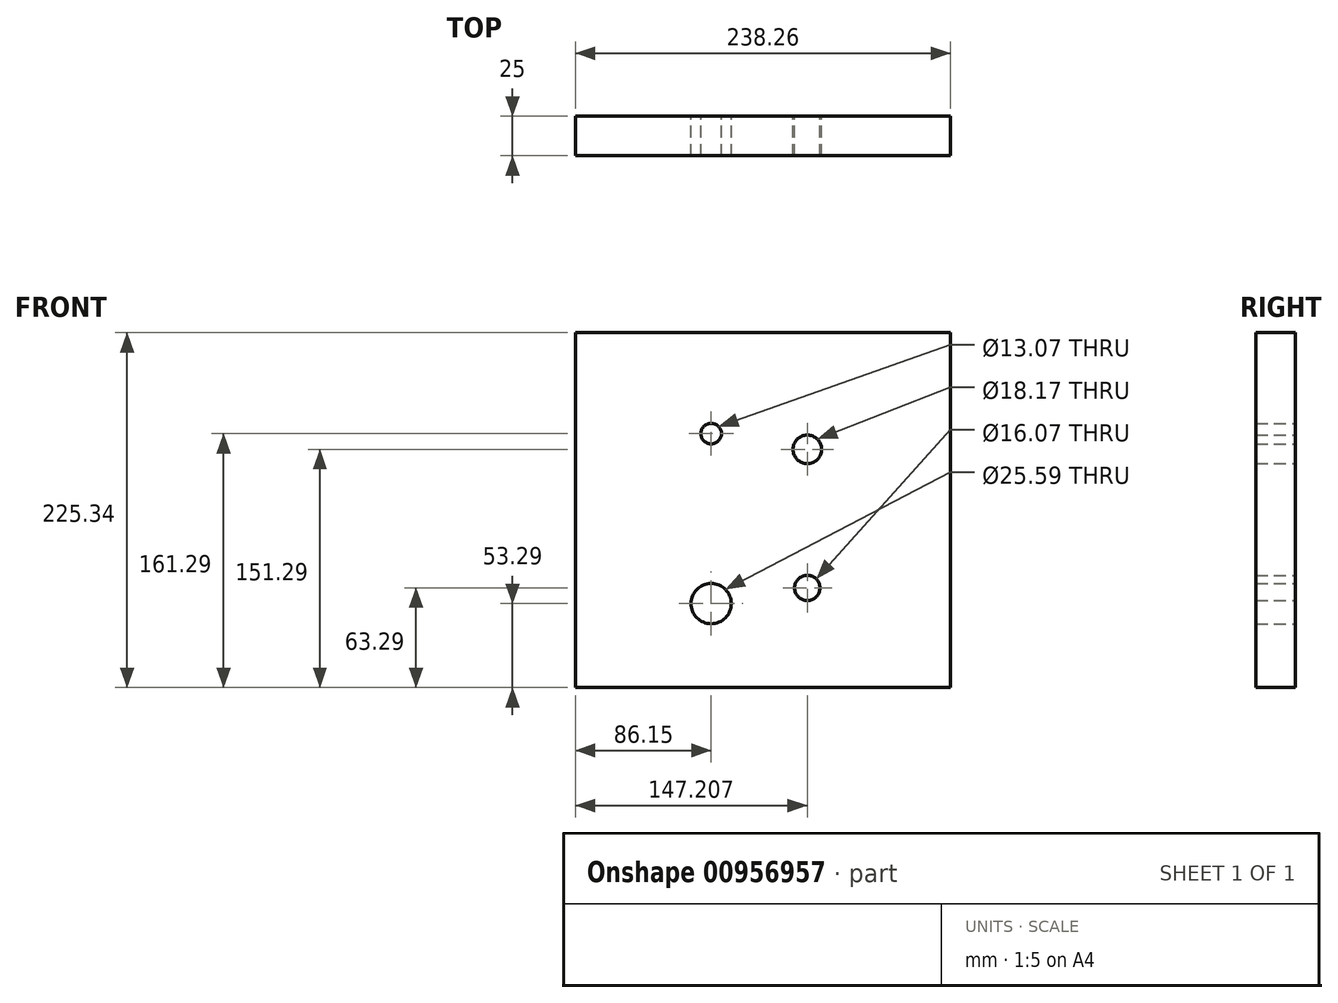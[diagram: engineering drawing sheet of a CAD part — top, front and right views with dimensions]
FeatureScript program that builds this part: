
annotation { "Feature Type Name" : "Feature", "Feature Type Description" : "" }
export const myFeature = defineFeature(function(context is Context, id is Id, definition is map)
    precondition{}
    {
        {
            var Q0;
            Q0=qCreatedBy(makeId("Front.planeOp"),FACE);
            var sketch = newSketch(context, id + "F0", { "sketchPlane" : qUnion([Q0])});
            skPoint(sketch, "E0", {"position": v(0, 0) * mm});
            skPoint(sketch, "E1", {"position": v(0, 108) * mm});
            skPoint(sketch, "E2", {"position": v(61.06, 98) * mm});
            skPoint(sketch, "E3", {"position": v(61.06, 10) * mm});
            skLineSegment(sketch, "E4.bottom", {"start": v(-86.15, 172.05) * mm, "end": v(152.1, 172.05) * mm});
            skLineSegment(sketch, "E4.top", {"start": v(-86.15, -53.29) * mm, "end": v(152.1, -53.29) * mm});
            skLineSegment(sketch, "E4.left", {"start": v(-86.15, 172.05) * mm, "end": v(-86.15, -53.29) * mm});
            skLineSegment(sketch, "E4.right", {"start": v(152.1, 172.05) * mm, "end": v(152.1, -53.29) * mm});
            skCircle(sketch, "E5", {"center": v(0, 108) * mm, "radius": 6.54 * mm});
            skCircle(sketch, "E6", {"center": v(61.06, 98) * mm, "radius": 9.08 * mm});
            skCircle(sketch, "E7", {"center": v(61.06, 10) * mm, "radius": 8.04 * mm});
            skCircle(sketch, "E8", {"center": v(0, 0) * mm, "radius": 12.8 * mm});
            skSolve(sketch);
        }
        {
            var Q0;
            Q0 = qSketchRegion(id + "F0", true);
            extrude(context, id + "F1", {"entities" : qUnion([Q0]), "depth" : 25 * mm, "offsetDistance" : 25 * mm});
        }
    });
